# Revit family: PRD_FrankeWS_WtrSpplFttngsFrWshBsnsAndTrghs_ElectronicThermostaticMixer_F5ET1001-1006
name_source: partatom
category: Plumbing Fixtures
revit_build: Autodesk Revit 2018 (Build: 20190510_1515(x64)
units: mm (PartAtom-declared; Revit-internal decimal feet)

## family parameters
Cut with Voids When Loaded = No
Host = Face
OmniClass Number = 23.45.55.17
OmniClass Title = Mixing Faucets
Part Type = Normal
Room Calculation Point = No
Round Connector Dimension = Use Diameter
Shared = No

## types (6) — shared parameters
AdjustableFlowTime = yes
AssetType = Fixed
Category = Pr_40_20_87_98, Washbasin taps
Color = Chrome
Default Elevation = 850 mm  [stored 2.78871 ft]
DefaultAutomaticHygieneFlushing = 24h after the last activity
DefaultFlowTime = 10.00 seconds
Depressurised = no
DiameterNominal = 15.000 mm
DurationUnit = year
FaucetFunction = MIXED
FaucetOperation = SELFCLOSING
FaucetType = BIB
Features = For sanitary facilities. For connection to hot and cold water.
Finish = high-polished chromium-plated brass
FlowColdWater = 0.1 L/s
FlowHotWater = 0.1 L/s
FunctionalPrinciple = electronic self-closing
HygieneFlushing = yes
IfcExportAs = IfcValveType
IfcExportType = FAUCET
InletSize = G-1-2-B
Manufacturer = KWC Group AG
ManufacturerName = KWC Group AG
ManufacturerURL = www.kwc.com
Material = Brass
MaterialsBody = Brass
MaximumFlowTime = 255.00 seconds
MinimumFlowPressure = 1.00 bar
MinimumFlowTime = 1.00 seconds
NBSDescription = Water supply fittings for wash basins and troughs
NBSReference = 45-35-70/371
NominalWidth = 305 mm  [stored 1.00066 ft]
OutletMaterial = PRD_AR_SyntheticGrey
PowerConsumption = 1.5
ProductInformation = https://pim.kwc.com
ProtectiveShutdown = yes
ProtectiveSystemIP = IP59K
SensorMaterial = PRD_AR_SyntheticDarkGrey
SoundInsulation = no
TapBottomOffset = 95 mm  [stored 0.31168 ft]
TapMaterial = PRD_AR_ChromatedBrass_HighPolished
ThermalDisinfection = prepared for automatic thermal disinfection
TypeOfMixing = with thermostat
TypeOfMounting = Wall mounting
TypeOfOperation = sensor operation
TypeOfSensor = opto-electronic sensor
TypeOfTap = bib tap
URL = www.kwc.com
Uniclass2015Code = Pr_40_20_87_98
Uniclass2015Title = Washbasin taps
Uniclass2015Version = Products v1.10
Version = 1
VolumeFlowRate = 0.10 L/s at 3 bar
VolumeFlowRateBypass = 0.05 liter per second
WarrantyDurationUnit = year
zero-valued in all types: NominalHeight, NominalLength

## per-type parameters (varying)
| type | BIMObjectName | Description | GrossWeight | LengthToSpout | Model | ModelNumber | ModelReference | Name | NetWeight | PositionOfPowerConnection | PowerSupplyConnection | SpoutProjection |
| F5ET1001 - 0.10 L/s with 6 V lithium battery, projection 155 mm | PRD_AR_WaterSupplyFittingsForWashBasinsAndTroughs_ElectronicThermostaticMixer_F5ET1001 | F5E-Therm thermostatic mixer DN 15 for wall mounting with lockable swivelling spout, for sanitary facilities. Opto-electronically controlled, triggered via hand movement. Thermostat with metal handle and adjustable, turn-proof temperature stop. With option for thermal disinfection, manually or automatically via optional disinfection unit. For connection to hot and cold water. Control electronics, solenoid valve cartridge, 6 V lithium battery (CR-P2) and sensor in scald-protected safe-touch housing, high-polished chromium-plated brass. Laminar jet controller with integrated flow regulator 6.0 l/min. With adjustable and lockable connections with backflow preventer and strainers, completely covered with depth-adjustable screw rosettes. Projection 155 mm. Activated water hygiene flushing 24 hours after last activation, safety switch-off with continuous reflection and saving of statistical data. With option for parameterization and communication via optional, bidirectional remote control. | 4.66 kg | 155 mm  [stored 0.50853 ft] | F5ET1001 | 2030032980 | F5ET1001 | F5 electronic thermostatic mixer F5ET1001 | 4.50 kg |  | Battery 6 V | 155.00 mm |
| F5ET1002 - 0.10 L/s with 6 V lithium battery, projection 215 mm | PRD_AR_WaterSupplyFittingsForWashBasinsAndTroughs_ElectronicThermostaticMixer_F5ET1002 | F5E-Therm thermostatic mixer DN 15 for wall mounting with lockable swivelling spout, for sanitary facilities. Opto-electronically controlled, triggered via hand movement. Thermostat with metal handle and adjustable, turn-proof temperature stop. With option for thermal disinfection, manually or automatically via optional disinfection unit. For connection to hot and cold water. Control electronics, solenoid valve cartridge, 6 V lithium battery (CR-P2) and sensor in scald-protected safe-touch housing, high-polished chromium-plated brass. Laminar jet controller with integrated flow regulator 6.0 l/min. With adjustable and lockable connections with backflow preventer and strainers, completely covered with depth-adjustable screw rosettes. Projection 215 mm. Activated water hygiene flushing 24 hours after last activation, safety switch-off with continuous reflection and saving of statistical data. With option for parameterization and communication via optional, bidirectional remote control. | 4.70 kg | 215 mm | F5ET1002 | 2030032981 | F5ET1002 | F5 electronic thermostatic mixer F5ET1002 | 4.50 kg |  | Battery 6 V | 215.00 mm |
| F5ET1003 - 0.10 L/s with 6 V lithium battery, projection 275 mm | PRD_AR_WaterSupplyFittingsForWashBasinsAndTroughs_ElectronicThermostaticMixer_F5ET1003 | F5E-Therm thermostatic mixer DN 15 for wall mounting with lockable swivelling spout, for sanitary facilities. Opto-electronically controlled, triggered via hand movement. Thermostat with metal handle and adjustable, turn-proof temperature stop. With option for thermal disinfection, manually or automatically via optional disinfection unit. For connection to hot and cold water. Control electronics, solenoid valve cartridge, 6 V lithium battery (CR-P2) and sensor in scald-protected safe-touch housing, high-polished chromium-plated brass. Laminar jet controller with integrated flow regulator 6.0 l/min. With adjustable and lockable connections with backflow preventer and strainers, completely covered with depth-adjustable screw rosettes. Projection 275 mm. Activated water hygiene flushing 24 hours after last activation, safety switch-off with continuous reflection and saving of statistical data. With option for parameterization and communication via optional, bidirectional remote control. | 4.90 kg | 275 mm | F5ET1003 | 2030032983 | F5ET1003 | F5 electronic thermostatic mixer F5ET1003 | 4.80 kg |  | Battery 6 V | 275.00 mm |
| F5ET1004 - 0.10 L/s with separate power supply via power supply unit 6.75 V / 12 V DC, projection 155 mm | PRD_AR_WaterSupplyFittingsForWashBasinsAndTroughs_ElectronicThermostaticMixer_F5ET1004 | F5E-Therm thermostatic mixer DN 15 for wall mounting with lockable swivelling spout, for sanitary facilities. Opto-electronically controlled, triggered via hand movement. Thermostat with metal handle with adjustable and turn-proof temperature stop. With option for thermal disinfection, manually or automatically via optional disinfection unit. For connection to hot and cold water. Control electronics, solenoid valve cartridge and sensor in scald-protected safe-touch housing, high-polished chromium-plated brass. Laminar jet controller with integrated flow regulator 6.0 l/min. With adjustable and lockable connections with backflow preventer and strainers, completely covered with depth-adjustable screw rosettes. Projection 155 mm. Activated water hygiene flushing 24 hours after last activation, safety switch-off with continuous reflection and saving of statistical data. With option for parameterization and communication via optional, bidirectional remote control. Separate power supply via power supply unit 6.75 V / 12 V DC or AQUA 3000 open system accessories. | 5.20 kg | 155 mm  [stored 0.50853 ft] | F5ET1004 | 2030036210 | F5ET1004 | F5 electronic thermostatic mixer F5ET1004 | 4.94 kg | from backside | 6,75 / 12 V DC / A3000 open | 155.00 mm |
| F5ET1005 - 0.10 L/s with separate power supply via power supply unit 6.75 V / 12 V DC, projection 215 mm | PRD_AR_WaterSupplyFittingsForWashBasinsAndTroughs_ElectronicThermostaticMixer_F5ET1005 | F5E-Therm thermostatic mixer DN 15 for wall mounting with lockable swivelling spout, for sanitary facilities. Opto-electronically controlled, triggered via hand movement. Thermostat with metal handle with adjustable and turn-proof temperature stop. With option for thermal disinfection, manually or automatically via optional disinfection unit. For connection to hot and cold water. Control electronics, solenoid valve cartridge and sensor in scald-protected safe-touch housing, high-polished chromium-plated brass. Laminar jet controller with integrated flow regulator 6.0 l/min. With adjustable and lockable connections with backflow preventer and strainers, completely covered with depth-adjustable screw rosettes. Projection 215 mm. Activated water hygiene flushing 24 hours after last activation, safety switch-off with continuous reflection and saving of statistical data. With option for parameterization and communication via optional, bidirectional remote control. Separate power supply via power supply unit 6.75 V / 12 V DC or AQUA 3000 open system accessories. | 5.20 kg | 215 mm | F5ET1005 | 2030036211 | F5ET1005 | F5 electronic thermostatic mixer F5ET1005 | 4.94 kg | from backside | 6,75 / 12 V DC / A3000 open | 215.00 mm |
| F5ET1006 - 0.10 L/s with separate power supply via power supply unit 6.75 V / 12 V DC, projection 275 mm | PRD_AR_WaterSupplyFittingsForWashBasinsAndTroughs_ElectronicThermostaticMixer_F5ET1006 | F5E-Therm thermostat wall mixer DN 15 for wall mounting with lockable swivelling spout, for sanitary facilities. Opto-electronically controlled, triggered via hand movement. Thermostat with metal handle with adjustable and turn-proof temperature stop. With option for thermal disinfection, manually or automatically via optional disinfection unit. For connection to hot and cold water. Control electronics, solenoid valve cartridge and sensor in scald-protected safe-touch housing, high-polished chromium-plated brass. Laminar jet controller with integrated flow regulator 6.0 l/min. With adjustable and lockable connections with backflow preventer and strainers, completely covered with depth-adjustable screw rosettes. Projection 275 mm. Activated water hygiene flushing 24 hours after last activation, safety switch-off with continuous reflection and saving of statistical data. With option for parameterization and communication via optional, bidirectional remote control. Separate power supply via power supply unit 6.75 V / 12 V DC or AQUA 3000 open system accessories. | 5.20 kg | 275 mm | F5ET1006 | 2030036212 | F5ET1006 | F5 electronic thermostatic mixer F5ET1006 | 4.94 kg | from backside | 6,75 / 12 V DC / A3000 open | 275.00 mm |

note: [stored X ft] marks values corroborated as IEEE doubles in the binary element streams (Revit-internal decimal feet)

## geometry (parser evidence)
native form markers: Sweep x2
no freeform markers — native parametric forms only
